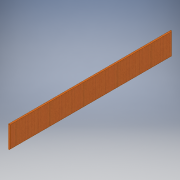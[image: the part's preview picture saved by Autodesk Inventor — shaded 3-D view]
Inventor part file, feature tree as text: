
AUTODESK INVENTOR PART (.ipt)
format: ipt  version: 2016 (Build 200138000, 138)  size: 107,520 bytes
history: native  units: in
note: dims shown in document units (in); Inventor stores cm internally (conversion verified against a paired STEP export)
features: extrude x1, fillet x1, sketch x1
ambient origin geometry x8: Origin, YZ Plane, XZ Plane, XY Plane, X Axis, Y Axis, Z Axis, Center Point
bodies: Solid1 (feature_tree)
feature tree (3):
  extrude  "Extrusion1"  Depth=6.5in
  fillet  "Fillet1"  Radius=0.4375in
  sketch  "Sketch1"  dims[d0=48.0in d1=6.5in d2=0.4375in d3=0.0in d4=0.125in]
